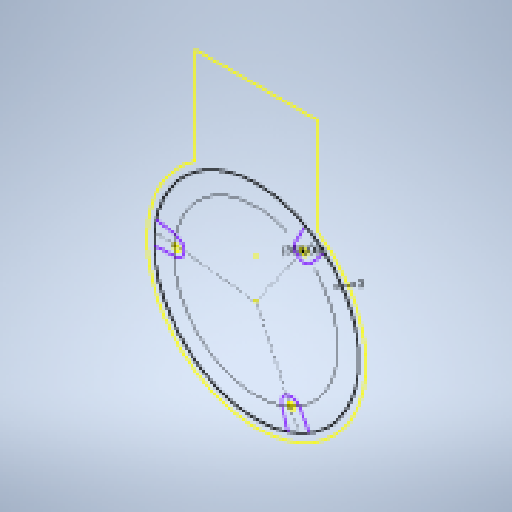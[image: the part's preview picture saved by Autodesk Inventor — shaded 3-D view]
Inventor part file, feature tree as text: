
AUTODESK INVENTOR PART (.ipt)
format: ipt  version: 2023 (Build 270158000, 158)  size: 180,736 bytes
history: native  units: mm
features: other x3, extrude x2, sketch x2
ambient origin geometry x8: Origin, YZ Plane, XZ Plane, XY Plane, X Axis, Y Axis, Z Axis, Center Point
bodies: Solide1 (feature_tree)
feature tree (7):
  extrude  "Extrusion1"  Depth=3.0mm
  extrude  "Extrusion2"  Depth=30.0mm TaperAngle=360.0deg
  sketch  "Esquisse1"
  other  "Référence1"
  sketch  "Esquisse2"
  other  "Ensemble1"
  other  "AnemoHolder:1"
